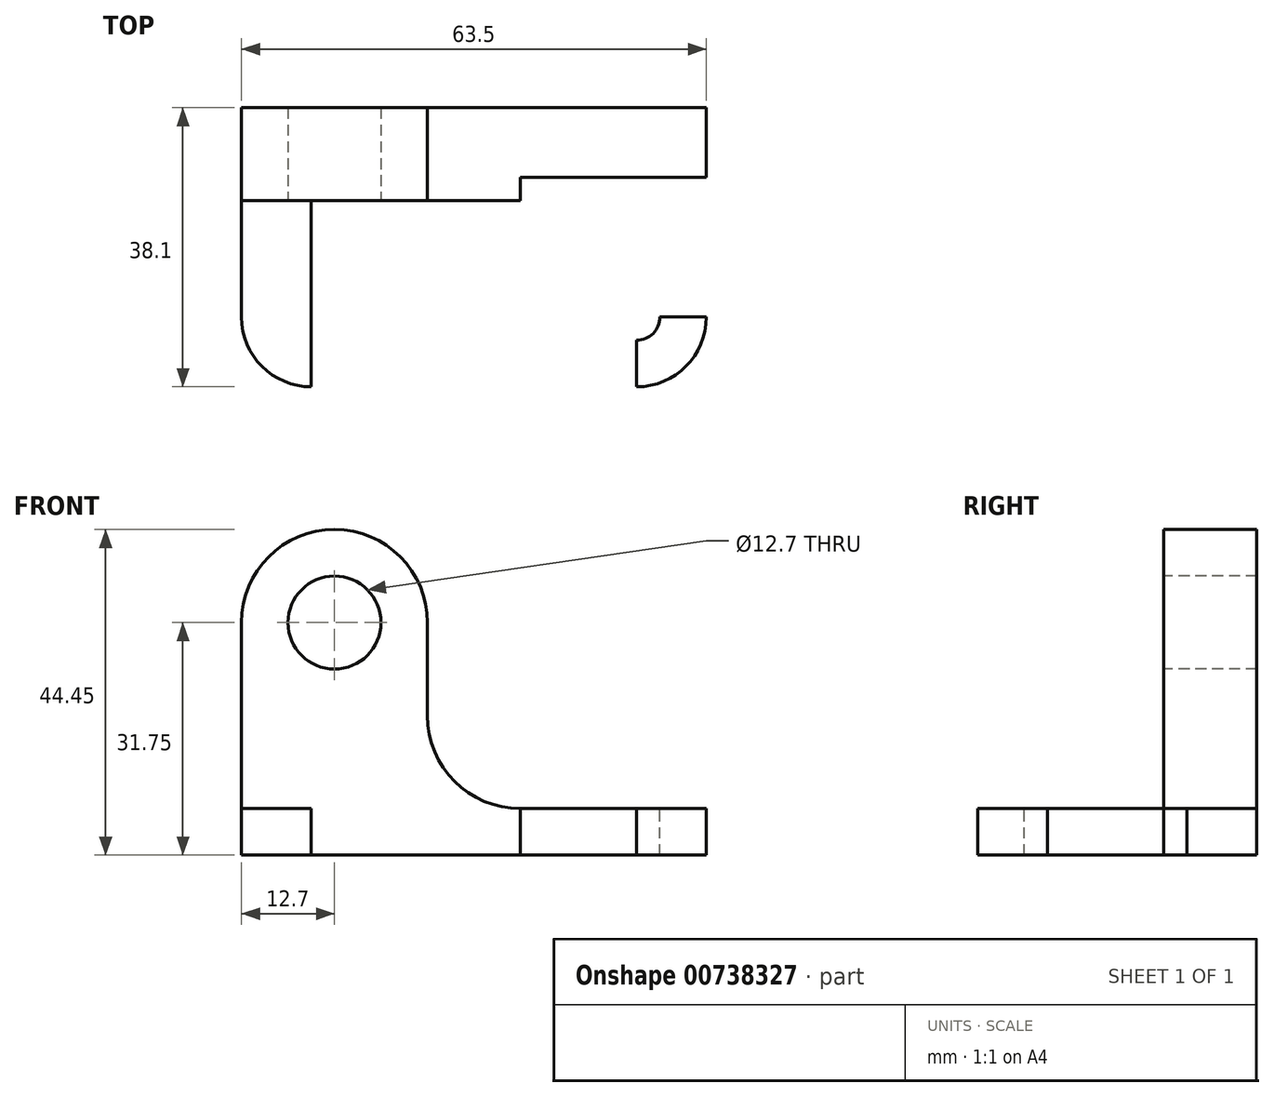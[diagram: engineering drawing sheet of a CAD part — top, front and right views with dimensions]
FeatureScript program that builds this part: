
annotation { "Feature Type Name" : "Feature", "Feature Type Description" : "" }
export const myFeature = defineFeature(function(context is Context, id is Id, definition is map)
    precondition{}
    {
        {
            var Q0;
            Q0=qCreatedBy(makeId("Right.planeOp"),FACE);
            var sketch = newSketch(context, id + "F0", { "sketchPlane" : qUnion([Q0])});
            skLineSegment(sketch, "E0", {"start": v(12.7, 0) * mm, "end": v(12.7, 44.45) * mm});
            skLineSegment(sketch, "E1", {"start": v(12.7, 44.45) * mm, "end": v(0, 44.45) * mm});
            skLineSegment(sketch, "E2", {"start": v(0, 44.45) * mm, "end": v(0, 6.35) * mm});
            skLineSegment(sketch, "E3", {"start": v(0, 6.35) * mm, "end": v(-25.4, 6.35) * mm});
            skLineSegment(sketch, "E4", {"start": v(-25.4, 6.35) * mm, "end": v(-25.4, 0) * mm});
            skLineSegment(sketch, "E5", {"start": v(-25.4, 0) * mm, "end": v(12.7, 0) * mm});
            skSolve(sketch);
        }
        {
            var Q0;
            Q0=makeQuery(id+"F0.imprint","IMPRINT",FACE,{"disambiguationData":[TD([[makeQuery(id+"F0.imprint","IMPRINT",EDGE,{"derivedFrom":sQuery(id+"F0.wireOp",EDGE,"E0")}),1.0]])]});
            extrude(context, id + "F1", {"entities" : qUnion([Q0]), "depth" : 63.5 * mm, "offsetDistance" : 25.4 * mm});
        }
        {
            var Q0;
            Q0=makeQuery(id+"F1.opExtrude","SWEPT_FACE",FACE,{"disambiguationData":[OSD([sQuery(id+"F0.wireOp",EDGE,"E2")])]});
            var sketch = newSketch(context, id + "F2", { "sketchPlane" : qUnion([Q0])});
            skLineSegment(sketch, "E6", {"start": v(38.1, 44.45) * mm, "end": v(38.1, 6.35) * mm});
            skLineSegment(sketch, "E7", {"start": v(38.1, 44.45) * mm, "end": v(63.5, 44.45) * mm});
            skLineSegment(sketch, "E8", {"start": v(0, 19.05) * mm, "end": v(63.5, 19.05) * mm});
            skLineSegment(sketch, "E9", {"start": v(63.5, 44.45) * mm, "end": v(63.5, 19.05) * mm});
            skCircle(sketch, "E10", {"center": v(38.1, 19.05) * mm, "radius": 12.7 * mm});
            skLineSegment(sketch, "E11", {"start": v(25.4, 19.05) * mm, "end": v(25.4, 44.45) * mm});
            skLineSegment(sketch, "E12", {"start": v(0, 31.75) * mm, "end": v(25.4, 31.75) * mm});
            skLineSegment(sketch, "E13", {"start": v(0, 44.45) * mm, "end": v(0, 31.75) * mm});
            skCircle(sketch, "E14", {"center": v(12.7, 31.75) * mm, "radius": 6.35 * mm});
            skArc(sketch, "E15", {"start": v(25.4, 31.75) * mm, "mid": v(12.7, 44.45) * mm, "end": v(0, 31.75) * mm});
            skSolve(sketch);
        }
        {
            var Q0;
            {var subQ4=sQuery(id+"F2.wireOp",EDGE,"E10");var subQ6=sQuery(id+"F2.wireOp",EDGE,"E6");var subQ8=makeQuery(id+"F2.imprint","INTERSECT",VERTEX,{"derivedFrom":[subQ6,subQ4]});Q0=makeQuery(id+"F2.imprint","IMPRINT",FACE,{"disambiguationData":[TD([[makeQuery(id+"F2.imprint","IMPRINT",EDGE,{"disambiguationData":[TD([[subQ8,-1.0]])],"derivedFrom":subQ4}),-1.0]])]});}
            var Q1;
            {var subQ5=sQuery(id+"F2.wireOp",EDGE,"E7");Q1=makeQuery(id+"F2.imprint","IMPRINT",FACE,{"disambiguationData":[TD([[makeQuery(id+"F2.imprint","IMPRINT",EDGE,{"derivedFrom":subQ5}),1.0]])]});}
            var Q2;
            {var subQ0=sQuery(id+"F2.wireOp",EDGE,"E10");var subQ1=sQuery(id+"F2.wireOp",EDGE,"E6");var subQ2=makeQuery(id+"F2.imprint","INTERSECT",VERTEX,{"derivedFrom":[subQ1,subQ0]});Q2=makeQuery(id+"F2.imprint","IMPRINT",FACE,{"disambiguationData":[TD([[makeQuery(id+"F2.imprint","IMPRINT",EDGE,{"disambiguationData":[TD([[subQ2,-1.0]])],"derivedFrom":subQ1}),1.0]])]});}
            var Q3;
            {var subQ0=sQuery(id+"F2.wireOp",EDGE,"E10");var subQ1=sQuery(id+"F2.wireOp",EDGE,"E6");var subQ2=makeQuery(id+"F2.imprint","INTERSECT",VERTEX,{"derivedFrom":[subQ1,subQ0]});Q3=makeQuery(id+"F2.imprint","IMPRINT",FACE,{"disambiguationData":[TD([[makeQuery(id+"F2.imprint","IMPRINT",EDGE,{"disambiguationData":[TD([[subQ2,-1.0]])],"derivedFrom":subQ1}),-1.0]])]});}
            var Q4;
            {var subQ1=sQuery(id+"F2.wireOp",EDGE,"E6");var subQ3=sQuery(id+"F2.wireOp",EDGE,"E8");var subQ4=makeQuery(id+"F2.imprint","INTERSECT",VERTEX,{"derivedFrom":[subQ1,subQ3]});Q4=makeQuery(id+"F2.imprint","IMPRINT",FACE,{"disambiguationData":[TD([[makeQuery(id+"F2.imprint","IMPRINT",EDGE,{"disambiguationData":[TD([[subQ4,1.0]])],"derivedFrom":subQ3}),-1.0]])]});}
            var Q5;
            {var subQ1=sQuery(id+"F2.wireOp",EDGE,"E6");var subQ3=sQuery(id+"F2.wireOp",EDGE,"E8");var subQ4=makeQuery(id+"F2.imprint","INTERSECT",VERTEX,{"derivedFrom":[subQ1,subQ3]});Q5=makeQuery(id+"F2.imprint","IMPRINT",FACE,{"disambiguationData":[TD([[makeQuery(id+"F2.imprint","IMPRINT",EDGE,{"disambiguationData":[TD([[subQ4,-1.0]])],"derivedFrom":subQ3}),-1.0]])]});}
            var Q6;
            {var subQ0=sQuery(id+"F2.wireOp",EDGE,"E8");var subQ4=sQuery(id+"F2.wireOp",EDGE,"E10");var subQ5=makeQuery(id+"F2.imprint","INTERSECT",VERTEX,{"derivedFrom":[subQ0,subQ4]});Q6=makeQuery(id+"F2.imprint","IMPRINT",FACE,{"disambiguationData":[TD([[makeQuery(id+"F2.imprint","IMPRINT",EDGE,{"disambiguationData":[TD([[subQ5,-1.0]])],"derivedFrom":subQ0}),-1.0]])]});}
            var Q7;
            {var subQ0=sQuery(id+"F2.wireOp",EDGE,"E11");var subQ1=makeQuery(id+"F1.opExtrude","SWEPT_EDGE",EDGE,{"disambiguationData":[OSD([sQuery(id+"F0.wireOp",EDGE,"E1"),sQuery(id+"F0.wireOp",EDGE,"E2")])]});var subQ2=makeQuery(id+"F2.imprint","INTERSECT",VERTEX,{"derivedFrom":[subQ1,subQ0]});Q7=makeQuery(id+"F2.imprint","IMPRINT",FACE,{"disambiguationData":[TD([[makeQuery(id+"F2.imprint","IMPRINT",EDGE,{"disambiguationData":[TD([[subQ2,1.0]])],"derivedFrom":subQ0}),1.0]])]});}
            var Q8;
            {var subQ0=sQuery(id+"F2.wireOp",EDGE,"E13");Q8=makeQuery(id+"F2.imprint","IMPRINT",FACE,{"disambiguationData":[TD([[makeQuery(id+"F2.imprint","IMPRINT",EDGE,{"derivedFrom":subQ0}),1.0]])]});}
            var Q9;
            {var subQ0=sQuery(id+"F2.wireOp",EDGE,"E14");var subQ1=sQuery(id+"F2.wireOp",EDGE,"E12");var subQ2=makeQuery(id+"F2.imprint","INTERSECT",VERTEX,{"disambiguationData":[OD(0.0)],"derivedFrom":[subQ1,subQ0]});Q9=makeQuery(id+"F2.imprint","IMPRINT",FACE,{"disambiguationData":[TD([[makeQuery(id+"F2.imprint","IMPRINT",EDGE,{"disambiguationData":[TD([[subQ2,-1.0]])],"derivedFrom":subQ1}),1.0]])]});}
            var Q10;
            {var subQ0=sQuery(id+"F2.wireOp",EDGE,"E14");var subQ1=sQuery(id+"F2.wireOp",EDGE,"E12");var subQ2=makeQuery(id+"F2.imprint","INTERSECT",VERTEX,{"disambiguationData":[OD(0.0)],"derivedFrom":[subQ1,subQ0]});Q10=makeQuery(id+"F2.imprint","IMPRINT",FACE,{"disambiguationData":[TD([[makeQuery(id+"F2.imprint","IMPRINT",EDGE,{"disambiguationData":[TD([[subQ2,-1.0]])],"derivedFrom":subQ1}),-1.0]])]});}
            extrude(context, id + "F3", {"entities" : qUnion([Q0, Q1, Q2, Q3, Q4, Q5, Q6, Q7, Q8, Q9, Q10]), "operationType" : NewBodyOperationType.REMOVE, "endBound" : BoundingType.THROUGH_ALL, "oppositeDirection" : true, "depth" : 25.4 * mm, "offsetDistance" : 25.4 * mm});
        }
        {
            var Q0;
            {var subQ0=sQuery(id+"F0.wireOp",EDGE,"E3");Q0=makeQuery(id+"F3.boolean.opBoolean","MERGE",FACE,{"derivedFrom":[makeQuery(id+"F1.opExtrude","SWEPT_FACE",FACE,{"disambiguationData":[OSD([subQ0])]}),makeQuery(id+"F3.opExtrude","SWEPT_FACE",FACE,{"disambiguationData":[OSD([sQuery(id+"F0.wireOp",EDGE,"E2"),subQ0])]})]});}
            var sketch = newSketch(context, id + "F4", { "sketchPlane" : qUnion([Q0])});
            skLineSegment(sketch, "E16", {"start": v(0, -15.87) * mm, "end": v(63.5, -15.87) * mm});
            skLineSegment(sketch, "E17", {"start": v(0, -15.87) * mm, "end": v(0, -25.4) * mm});
            skLineSegment(sketch, "E18", {"start": v(63.5, -25.4) * mm, "end": v(53.98, -25.4) * mm});
            skLineSegment(sketch, "E19", {"start": v(53.98, 12.7) * mm, "end": v(53.98, -25.4) * mm});
            skCircle(sketch, "E20", {"center": v(53.98, -15.87) * mm, "radius": 3.18 * mm});
            skLineSegment(sketch, "E21", {"start": v(0, -25.4) * mm, "end": v(9.53, -25.4) * mm});
            skLineSegment(sketch, "E22", {"start": v(9.53, -25.4) * mm, "end": v(9.53, 0) * mm});
            skCircle(sketch, "E23", {"center": v(9.52, -15.87) * mm, "radius": 3.18 * mm});
            skLineSegment(sketch, "E24", {"start": v(63.5, 12.7) * mm, "end": v(63.5, 3.18) * mm});
            skLineSegment(sketch, "E25", {"start": v(63.5, 3.18) * mm, "end": v(38.1, 3.18) * mm});
            skCircle(sketch, "E26", {"center": v(53.98, 3.18) * mm, "radius": 3.18 * mm});
            skArc(sketch, "E27", {"start": v(0, -15.87) * mm, "mid": v(2.79, -22.61) * mm, "end": v(9.53, -25.4) * mm});
            skArc(sketch, "E28", {"start": v(53.98, -25.4) * mm, "mid": v(60.71, -22.61) * mm, "end": v(63.5, -15.87) * mm});
            skSolve(sketch);
        }
        {
            var Q0;
            {var subQ0=sQuery(id+"F4.wireOp",EDGE,"E26");var subQ1=sQuery(id+"F4.wireOp",EDGE,"E19");var subQ2=makeQuery(id+"F4.imprint","INTERSECT",VERTEX,{"disambiguationData":[OD(0.0)],"derivedFrom":[subQ1,subQ0]});Q0=makeQuery(id+"F4.imprint","IMPRINT",FACE,{"disambiguationData":[TD([[makeQuery(id+"F4.imprint","IMPRINT",EDGE,{"disambiguationData":[TD([[subQ2,-1.0]])],"derivedFrom":subQ1}),1.0]])]});}
            var Q1;
            {var subQ0=sQuery(id+"F4.wireOp",EDGE,"E26");var subQ1=sQuery(id+"F4.wireOp",EDGE,"E19");var subQ2=makeQuery(id+"F4.imprint","INTERSECT",VERTEX,{"disambiguationData":[OD(0.0)],"derivedFrom":[subQ1,subQ0]});Q1=makeQuery(id+"F4.imprint","IMPRINT",FACE,{"disambiguationData":[TD([[makeQuery(id+"F4.imprint","IMPRINT",EDGE,{"disambiguationData":[TD([[subQ2,-1.0]])],"derivedFrom":subQ1}),-1.0]])]});}
            var Q2;
            {var subQ0=sQuery(id+"F4.wireOp",EDGE,"E25");var subQ1=sQuery(id+"F4.wireOp",EDGE,"E19");var subQ2=makeQuery(id+"F4.imprint","INTERSECT",VERTEX,{"derivedFrom":[subQ1,subQ0]});Q2=makeQuery(id+"F4.imprint","IMPRINT",FACE,{"disambiguationData":[TD([[makeQuery(id+"F4.imprint","IMPRINT",EDGE,{"disambiguationData":[TD([[subQ2,-1.0]])],"derivedFrom":subQ1}),-1.0]])]});}
            var Q3;
            {var subQ0=sQuery(id+"F4.wireOp",EDGE,"E25");var subQ1=sQuery(id+"F4.wireOp",EDGE,"E19");var subQ2=makeQuery(id+"F4.imprint","INTERSECT",VERTEX,{"derivedFrom":[subQ1,subQ0]});Q3=makeQuery(id+"F4.imprint","IMPRINT",FACE,{"disambiguationData":[TD([[makeQuery(id+"F4.imprint","IMPRINT",EDGE,{"disambiguationData":[TD([[subQ2,-1.0]])],"derivedFrom":subQ1}),1.0]])]});}
            var Q4;
            {var subQ0=sQuery(id+"F4.wireOp",EDGE,"E19");var subQ1=sQuery(id+"F4.wireOp",EDGE,"E16");var subQ2=makeQuery(id+"F4.imprint","INTERSECT",VERTEX,{"derivedFrom":[subQ1,subQ0]});Q4=makeQuery(id+"F4.imprint","IMPRINT",FACE,{"disambiguationData":[TD([[makeQuery(id+"F4.imprint","IMPRINT",EDGE,{"disambiguationData":[TD([[subQ2,-1.0]])],"derivedFrom":subQ1}),1.0]])]});}
            var Q5;
            {var subQ0=sQuery(id+"F4.wireOp",EDGE,"E20");var subQ1=sQuery(id+"F4.wireOp",EDGE,"E16");var subQ2=makeQuery(id+"F4.imprint","INTERSECT",VERTEX,{"disambiguationData":[OD(0.0)],"derivedFrom":[subQ1,subQ0]});Q5=makeQuery(id+"F4.imprint","IMPRINT",FACE,{"disambiguationData":[TD([[makeQuery(id+"F4.imprint","IMPRINT",EDGE,{"disambiguationData":[TD([[subQ2,-1.0]])],"derivedFrom":subQ1}),1.0]])]});}
            var Q6;
            {var subQ0=sQuery(id+"F4.wireOp",EDGE,"E20");var subQ1=sQuery(id+"F4.wireOp",EDGE,"E16");var subQ2=makeQuery(id+"F4.imprint","INTERSECT",VERTEX,{"disambiguationData":[OD(0.0)],"derivedFrom":[subQ1,subQ0]});Q6=makeQuery(id+"F4.imprint","IMPRINT",FACE,{"disambiguationData":[TD([[makeQuery(id+"F4.imprint","IMPRINT",EDGE,{"disambiguationData":[TD([[subQ2,-1.0]])],"derivedFrom":subQ1}),-1.0]])]});}
            var Q7;
            {var subQ0=sQuery(id+"F4.wireOp",EDGE,"E19");var subQ1=sQuery(id+"F4.wireOp",EDGE,"E16");var subQ2=makeQuery(id+"F4.imprint","INTERSECT",VERTEX,{"derivedFrom":[subQ1,subQ0]});Q7=makeQuery(id+"F4.imprint","IMPRINT",FACE,{"disambiguationData":[TD([[makeQuery(id+"F4.imprint","IMPRINT",EDGE,{"disambiguationData":[TD([[subQ2,-1.0]])],"derivedFrom":subQ1}),-1.0]])]});}
            var Q8;
            {var subQ0=sQuery(id+"F4.wireOp",EDGE,"E18");Q8=makeQuery(id+"F4.imprint","IMPRINT",FACE,{"disambiguationData":[TD([[makeQuery(id+"F4.imprint","IMPRINT",EDGE,{"derivedFrom":subQ0}),-1.0]])]});}
            var Q9;
            Q9=makeQuery(id+"F4.imprint","IMPRINT",FACE,{"disambiguationData":[TD([[makeQuery(id+"F4.imprint","IMPRINT",EDGE,{"derivedFrom":sQuery(id+"F4.wireOp",EDGE,"E17")}),1.0]])]});
            var Q10;
            {var subQ0=sQuery(id+"F4.wireOp",EDGE,"E23");var subQ1=sQuery(id+"F4.wireOp",EDGE,"E16");var subQ2=makeQuery(id+"F4.imprint","INTERSECT",VERTEX,{"disambiguationData":[OD(0.0)],"derivedFrom":[subQ1,subQ0]});Q10=makeQuery(id+"F4.imprint","IMPRINT",FACE,{"disambiguationData":[TD([[makeQuery(id+"F4.imprint","IMPRINT",EDGE,{"disambiguationData":[TD([[subQ2,-1.0]])],"derivedFrom":subQ1}),-1.0]])]});}
            var Q11;
            {var subQ0=sQuery(id+"F4.wireOp",EDGE,"E23");var subQ1=sQuery(id+"F4.wireOp",EDGE,"E16");var subQ2=makeQuery(id+"F4.imprint","INTERSECT",VERTEX,{"disambiguationData":[OD(0.0)],"derivedFrom":[subQ1,subQ0]});Q11=makeQuery(id+"F4.imprint","IMPRINT",FACE,{"disambiguationData":[TD([[makeQuery(id+"F4.imprint","IMPRINT",EDGE,{"disambiguationData":[TD([[subQ2,-1.0]])],"derivedFrom":subQ1}),1.0]])]});}
            var Q12;
            {var subQ0=sQuery(id+"F4.wireOp",EDGE,"E22");var subQ1=sQuery(id+"F4.wireOp",EDGE,"E16");var subQ2=makeQuery(id+"F4.imprint","INTERSECT",VERTEX,{"derivedFrom":[subQ1,subQ0]});Q12=makeQuery(id+"F4.imprint","IMPRINT",FACE,{"disambiguationData":[TD([[makeQuery(id+"F4.imprint","IMPRINT",EDGE,{"disambiguationData":[TD([[subQ2,-1.0]])],"derivedFrom":subQ1}),1.0]])]});}
            var Q13;
            {var subQ0=sQuery(id+"F4.wireOp",EDGE,"E22");var subQ1=sQuery(id+"F4.wireOp",EDGE,"E16");var subQ2=makeQuery(id+"F4.imprint","INTERSECT",VERTEX,{"derivedFrom":[subQ1,subQ0]});Q13=makeQuery(id+"F4.imprint","IMPRINT",FACE,{"disambiguationData":[TD([[makeQuery(id+"F4.imprint","IMPRINT",EDGE,{"disambiguationData":[TD([[subQ2,-1.0]])],"derivedFrom":subQ1}),-1.0]])]});}
            extrude(context, id + "F5", {"entities" : qUnion([Q0, Q1, Q2, Q3, Q4, Q5, Q6, Q7, Q8, Q9, Q10, Q11, Q12, Q13]), "operationType" : NewBodyOperationType.REMOVE, "endBound" : BoundingType.THROUGH_ALL, "oppositeDirection" : true, "depth" : 25.4 * mm, "offsetDistance" : 25.4 * mm});
        }
    });
